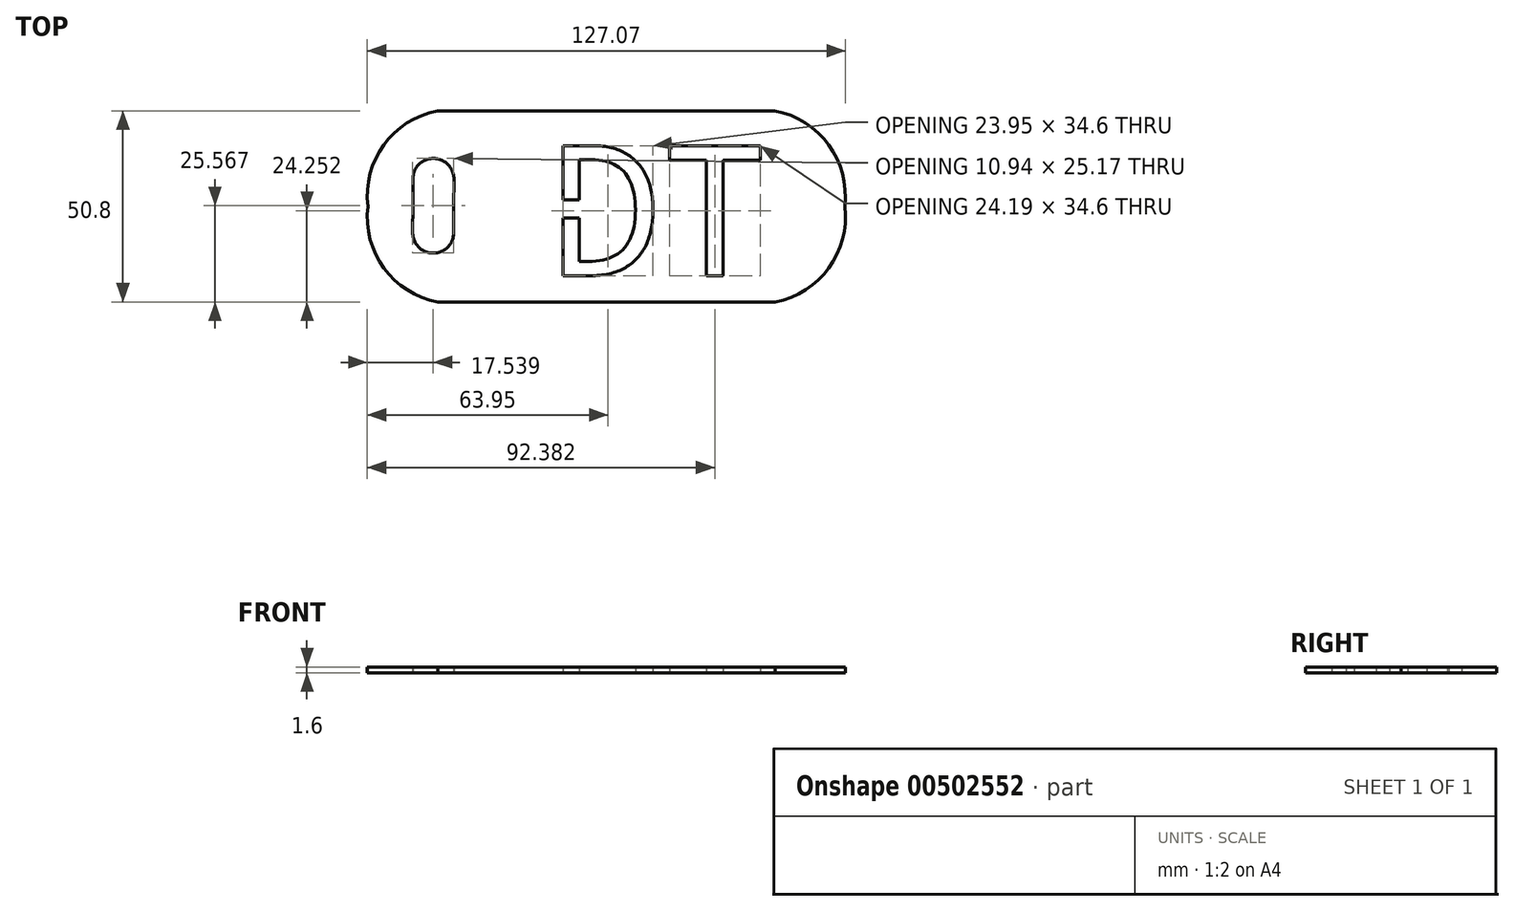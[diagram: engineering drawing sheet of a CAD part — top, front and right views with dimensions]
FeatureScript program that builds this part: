
annotation { "Feature Type Name" : "Feature", "Feature Type Description" : "" }
export const myFeature = defineFeature(function(context is Context, id is Id, definition is map)
    precondition{}
    {
        {
            var Q0;
            Q0=qCreatedBy(makeId("Top.planeOp"),FACE);
            var sketch = newSketch(context, id + "F0", { "sketchPlane" : qUnion([Q0])});
            skLineSegment(sketch, "E0.bottom", {"start": v(44.6, 25.4) * mm, "end": v(-45, 25.4) * mm});
            skLineSegment(sketch, "E0.top", {"start": v(44.71, -25.4) * mm, "end": v(-44.9, -25.4) * mm});
            skLineSegment(sketch, "E0.right", {"start": v(-63.5, 5.7) * mm, "end": v(-63.5, 0) * mm});
            skPoint(sketch, "E0.middle", {"position": v(0, 0) * mm});
            skArc(sketch, "E1", {"start": v(-63.5, 0) * mm, "mid": v(-59.24, -16.4) * mm, "end": v(-44.9, -25.4) * mm});
            skArc(sketch, "E2", {"start": v(-44.92, 25.42) * mm, "mid": v(-59.25, 16.4) * mm, "end": v(-63.5, 0) * mm});
            skArc(sketch, "E3", {"start": v(63.21, 0) * mm, "mid": v(58.95, 16.4) * mm, "end": v(44.6, 25.4) * mm});
            skArc(sketch, "E4", {"start": v(44.63, -25.42) * mm, "mid": v(58.97, -16.4) * mm, "end": v(63.21, 0) * mm});
            skPoint(sketch, "E5.orphan", {"position": v(-63.5, 25.4) * mm});
            skPoint(sketch, "E6.orphan", {"position": v(-63.5, -25.4) * mm});
            skPoint(sketch, "E0.left.end.orphan", {"position": v(63.5, -25.4) * mm});
            skPoint(sketch, "E7.orphan", {"position": v(63.5, 25.4) * mm});
            skText(sketch, "E8", { "text": "DT", "fontName": "DroidSansMono.ttf"});
            skLineSegment(sketch, "E9.left", {"start": v(-40.67, 6.89) * mm, "end": v(-40.67, 7.69) * mm});
            skLineSegment(sketch, "E9.right", {"start": v(-51.56, 0) * mm, "end": v(-51.56, 7.69) * mm});
            skPoint(sketch, "E10.firstSnap0", {"position": v(-51.56, 0.33) * mm});
            skPoint(sketch, "E10.oppositeSnap0", {"position": v(-51.56, 0.33) * mm});
            skLineSegment(sketch, "E10.left", {"start": v(-51.56, 0) * mm, "end": v(-51.56, 0.33) * mm});
            skLineSegment(sketch, "E10.right", {"start": v(-40.72, 0) * mm, "end": v(-40.72, 0.33) * mm});
            skArc(sketch, "E11", {"start": v(-40.67, 6.89) * mm, "mid": v(-46.12, 12.75) * mm, "end": v(-51.56, 6.89) * mm});
            skPoint(sketch, "E12.orphan", {"position": v(-51.56, 13.56) * mm});
            skPoint(sketch, "E9.bottom.end.orphan", {"position": v(-51.56, -12.9) * mm});
            skLineSegment(sketch, "E13", {"start": v(-40.72, 0.33) * mm, "end": v(-40.67, 6.89) * mm});
            skLineSegment(sketch, "E14.right", {"start": v(-40.72, 0.33) * mm, "end": v(-40.72, -7.36) * mm});
            skArc(sketch, "E15", {"start": v(-51.6, -6.56) * mm, "mid": v(-46.16, -12.42) * mm, "end": v(-40.72, -6.56) * mm});
            skLineSegment(sketch, "E16", {"start": v(-51.56, 0) * mm, "end": v(-51.6, -6.56) * mm});
            skLineSegment(sketch, "E17.top", {"start": v(0, 1.78) * mm, "end": v(-14.9, 1.78) * mm});
            skLineSegment(sketch, "E17.left", {"start": v(0, 0) * mm, "end": v(0, 1.78) * mm});
            skLineSegment(sketch, "E17.right", {"start": v(-14.9, 0) * mm, "end": v(-14.9, 1.78) * mm});
            skLineSegment(sketch, "E18.bottom", {"start": v(0, 0) * mm, "end": v(-14.9, 0) * mm});
            skLineSegment(sketch, "E18.top", {"start": v(0, -3.11) * mm, "end": v(-14.9, -3.11) * mm});
            skLineSegment(sketch, "E18.left", {"start": v(0, 0) * mm, "end": v(0, -3.11) * mm});
            skLineSegment(sketch, "E18.right", {"start": v(-14.9, 0) * mm, "end": v(-14.9, -3.11) * mm});
            const initialGuessF0  = {"E8": [-0.0149, -0.01845, 1, 0, 0.0349]};
            skSetInitialGuess(sketch, initialGuessF0);
            skSolve(sketch);
        }
        {
            var Q0;
            {var subQ0=sQuery(id+"F0.wireOp",EDGE,"E0.right");Q0=makeQuery(id+"F0.imprint","IMPRINT",FACE,{"disambiguationData":[TD([[makeQuery(id+"F0.imprint","IMPRINT",EDGE,{"derivedFrom":subQ0}),-1.0]])]});}
            var Q1;
            {var subQ5=sQuery(id+"F0.wireOp",EDGE,"E17.right");Q1=makeQuery(id+"F0.imprint","IMPRINT",FACE,{"disambiguationData":[TD([[makeQuery(id+"F0.imprint","IMPRINT",EDGE,{"derivedFrom":subQ5}),-1.0]])]});}
            var Q2;
            {var subQ5=sQuery(id+"F0.wireOp",EDGE,"E18.right");Q2=makeQuery(id+"F0.imprint","IMPRINT",FACE,{"disambiguationData":[TD([[makeQuery(id+"F0.imprint","IMPRINT",EDGE,{"derivedFrom":subQ5}),1.0]])]});}
            var Q3;
            {var subQ0=sQuery(id+"F0.wireOp",EDGE,"E18.top");var subQ1=sQuery(id+"F0.wireOp",EDGE,"E8.sketch_text.stroke-0");var subQ2=makeQuery(id+"F0.imprint","INTERSECT",VERTEX,{"derivedFrom":[subQ1,subQ0]});Q3=makeQuery(id+"F0.imprint","IMPRINT",FACE,{"disambiguationData":[TD([[makeQuery(id+"F0.imprint","IMPRINT",EDGE,{"disambiguationData":[TD([[subQ2,-1.0]])],"derivedFrom":subQ1}),-1.0]])]});}
            var Q4;
            {var subQ0=sQuery(id+"F0.wireOp",EDGE,"E18.bottom");var subQ1=sQuery(id+"F0.wireOp",EDGE,"E8.sketch_text.stroke-0");var subQ2=makeQuery(id+"F0.imprint","INTERSECT",VERTEX,{"derivedFrom":[subQ1,subQ0]});Q4=makeQuery(id+"F0.imprint","IMPRINT",FACE,{"disambiguationData":[TD([[makeQuery(id+"F0.imprint","IMPRINT",EDGE,{"disambiguationData":[TD([[subQ2,-1.0]])],"derivedFrom":subQ1}),-1.0]])]});}
            var Q5;
            {var subQ5=sQuery(id+"F0.wireOp",EDGE,"E18.left");Q5=makeQuery(id+"F0.imprint","IMPRINT",FACE,{"disambiguationData":[TD([[makeQuery(id+"F0.imprint","IMPRINT",EDGE,{"derivedFrom":subQ5}),-1.0]])]});}
            var Q6;
            {var subQ5=sQuery(id+"F0.wireOp",EDGE,"E17.left");Q6=makeQuery(id+"F0.imprint","IMPRINT",FACE,{"disambiguationData":[TD([[makeQuery(id+"F0.imprint","IMPRINT",EDGE,{"derivedFrom":subQ5}),1.0]])]});}
            var Q7;
            {var subQ0=sQuery(id+"F0.wireOp",EDGE,"E8.sketch_text.stroke-8");Q7=makeQuery(id+"F0.imprint","IMPRINT",FACE,{"disambiguationData":[TD([[makeQuery(id+"F0.imprint","IMPRINT",EDGE,{"derivedFrom":subQ0}),1.0]])]});}
            var Q8;
            {var subQ9=sQuery(id+"F0.wireOp",EDGE,"E0.bottom");Q8=makeQuery(id+"F0.imprint","IMPRINT",FACE,{"disambiguationData":[TD([[makeQuery(id+"F0.imprint","IMPRINT",EDGE,{"derivedFrom":subQ9}),1.0]])]});}
            extrude(context, id + "F1", {"entities" : qUnion([Q0, Q1, Q2, Q3, Q4, Q5, Q6, Q7, Q8]), "depth" : 1.6 * mm});
        }
    });
